# Revit family: xLIFE-xx-xx-WP_V1.0_Non-Hosted_R16
name_source: partatom
category: Lighting Fixtures
revit_build: Autodesk Revit 2016 (Build: 20151007_0715(x64)
units: mm (PartAtom-declared; Revit-internal decimal feet)

## family parameters
Always vertical = Yes
Cut with Voids When Loaded = No
Light Source = Yes
OmniClass Number = 23.80.70.00
OmniClass Title = Lighting
Part Type = Normal
Room Calculation Point = No
Round Connector Dimension = Use Diameter
Shared = No
Work Plane-Based = No

## types (2) — shared parameters
AS2293 Classification = C0=D50 C90=D50
Battery = 3.2V 3200mAh
Battery Type = Lithium Iron Phosphate
Charging Method = Intelligent Current Limited Constant Voltage
Color Filter = 16777215
Construction = Polycarbonate Enclosure
Dimensions (L x W x H) = 247mm x 129mm x 51mm
Dimming Lamp Color Temperature Shift = <None>
Emit Shape Visible in Rendering = No
Emit from Rectangle Length = 1219 mm
Emit from Rectangle Width = 610 mm
IK Rating = IK08
IP Rating = IP65
Manufacturer = Clevertronics
Mounting = Surface Mounted
Operating Mode = Non-maintained
Operating Voltage = 240V AC; 50Hz
Replacement lamp = 8050174 Lifelight Head: CT10694-D1
Tilt Angle = 90.00°
Weight = 0.8kg

## per-type parameters (varying)
| type | Lamp | MIC Number | Operating Temperature | Photometric Web File | Power Consumption | Power Consumption (Standby) | Product Description | Replacement Battery | Replacement Driver | Testing System |
| ELIFE-X-LI-SM-WP | LED (Lifetime warranty on the lamp head and loom assembly) | AUD03520010001 | 1˚C to 40˚C | 200234PH_A1(ELIFE-X-LI-SM-WP,AS2293.3,Classification).ies | 1.3W | 0.4W | Economy Lithium Lifelight, Weatherproof, Surface Mounted Emergency Light | 1560160 BATT:EcoLith 3.2V 3.0Ah 170mm lead,NoBKT | 8002986 PCA: ELIFE-X-SMS-LI CT10614-L2 | Manual test switch |
| CLIFE-SM-WP | 1 x High intensity LED | AUD02320020001 | 0˚C to 40˚C | 200250PH(CLIFE-SM-WP-HV,AS2293.3,Photometry).ies | 4.2W (Max) | 1W | LP Premium Lifelight, Weatherproof, Surface Mounted Emergency Light, Enabled with
Clevertest Plus | 1550030 BATT:LP 3.2V 3200mAh 260mm lead,noBRKT. | 8002934 Driver: PCA: CLIFE CT10260-L5 1C650 CTP AU Vert Connectors | Clevertest Plus Enabled (Not activated by default) |

note: column(s) folded — value = type name in every type: Model

## geometry (parser evidence)
native form markers: Sweep x2
no freeform markers — native parametric forms only
